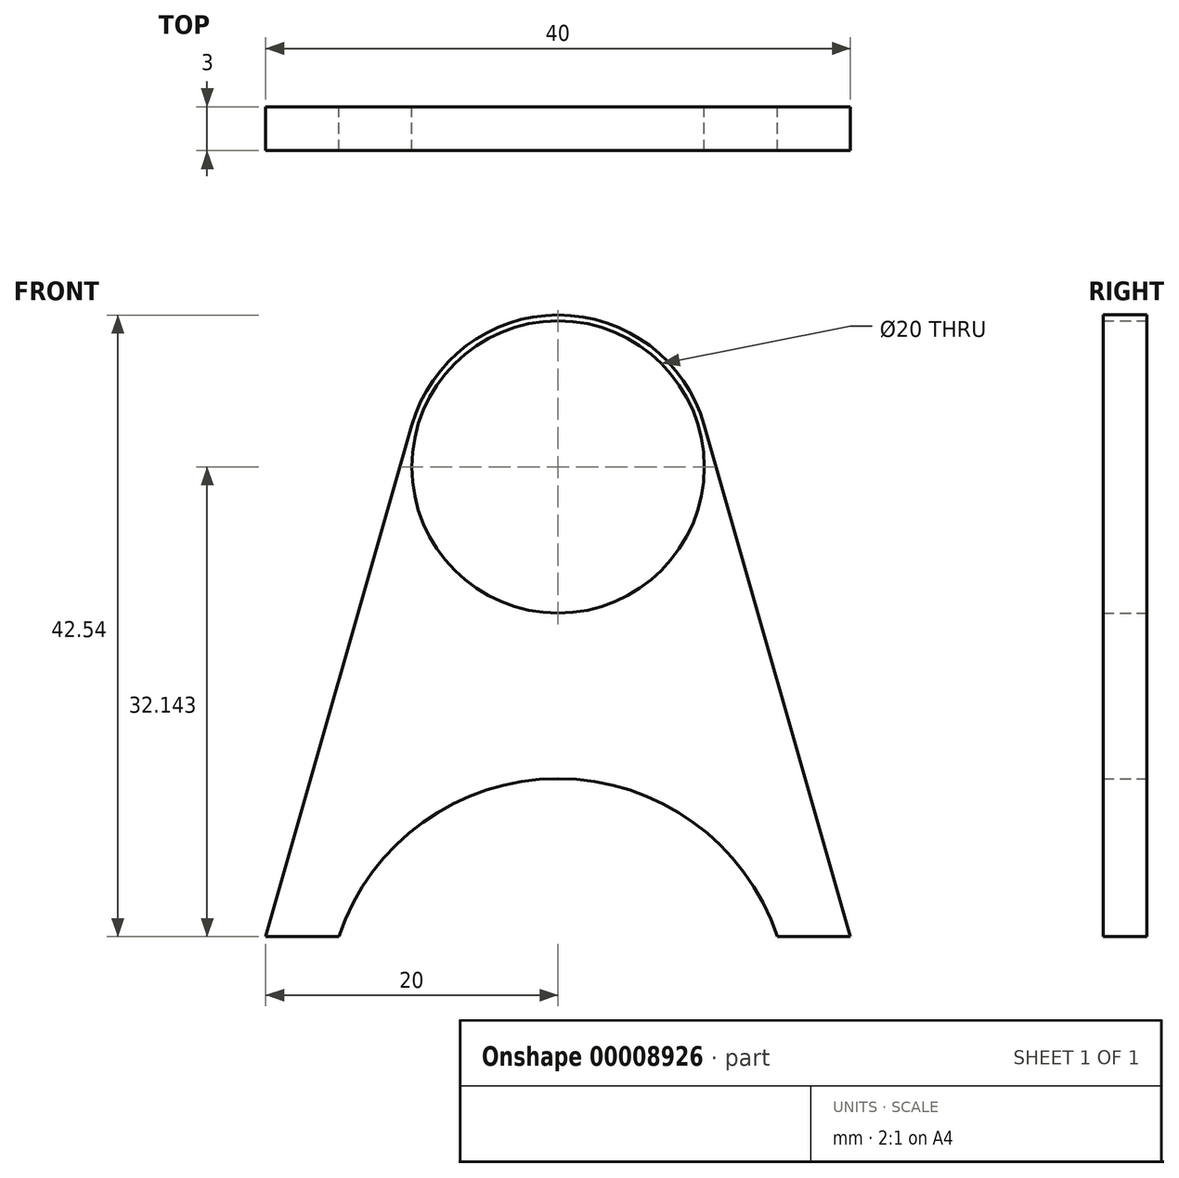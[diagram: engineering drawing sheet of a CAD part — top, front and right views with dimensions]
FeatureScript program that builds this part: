
annotation { "Feature Type Name" : "Feature", "Feature Type Description" : "" }
export const myFeature = defineFeature(function(context is Context, id is Id, definition is map)
    precondition{}
    {
        {
            var Q0;
            Q0=qCreatedBy(makeId("Front.planeOp"),FACE);
            var sketch = newSketch(context, id + "F0", { "sketchPlane" : qUnion([Q0])});
            skLineSegment(sketch, "E0", {"start": v(-20, 0) * mm, "end": v(-15, 0) * mm});
            skLineSegment(sketch, "E1", {"start": v(15, 0) * mm, "end": v(20, 0) * mm});
            skArc(sketch, "E2", {"start": v(15, 0) * mm, "mid": v(0, 10.81) * mm, "end": v(-15, 0) * mm});
            skLineSegment(sketch, "E3", {"start": v(-20, 0) * mm, "end": v(-10, 35) * mm});
            skLineSegment(sketch, "E4", {"start": v(20, 0) * mm, "end": v(10, 35) * mm});
            skArc(sketch, "E5", {"start": v(10, 35) * mm, "mid": v(0, 42.54) * mm, "end": v(-10, 35) * mm});
            skCircle(sketch, "E6", {"center": v(0, 32.14) * mm, "radius": 10 * mm});
            skSolve(sketch);
        }
        {
            var Q0;
            Q0 = qSketchRegion(id + "F0", true);
            extrude(context, id + "F1", {"entities" : qUnion([Q0]), "depth" : 3 * mm});
        }
    });
